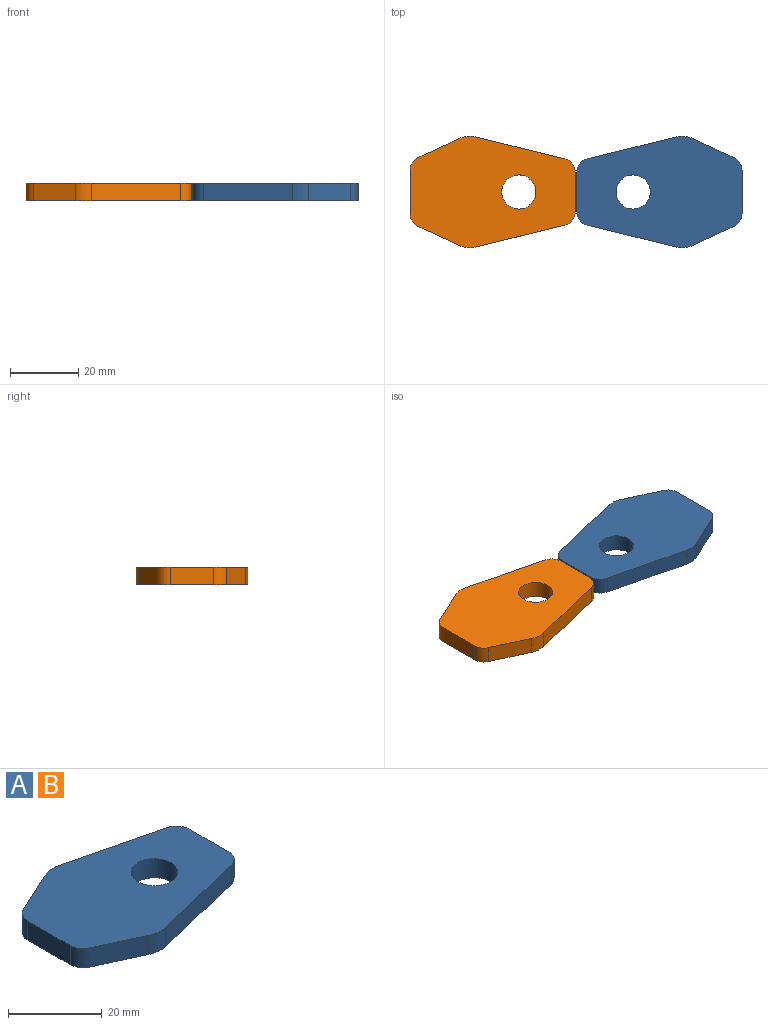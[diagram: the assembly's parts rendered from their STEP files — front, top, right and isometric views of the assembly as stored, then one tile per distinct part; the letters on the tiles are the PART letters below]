
ASSEMBLY  parts=2 mates=1
PART A: 15 faces, bbox 48.4x32.7x5 mm
  f0: cylinder r=7mm len=5mm, axis (0,0,-1), area 23.4mm2, adj f1,f7,f9,f10
  f1: plane 12.21x5.61mm, normal (-0.42,0.91,0), area 67.2mm2, adj f0,f9,f10,f11
  f2: plane 12.87x5mm, normal (-1,0,0), area 64.4mm2, adj f9,f10,f11,f12
  f3: plane 12.21x5.61mm, normal (-0.42,-0.91,0), area 67.2mm2, adj f4,f9,f10,f12
  f4: cylinder r=7mm len=5mm, axis (0,0,-1), area 23.4mm2, adj f3,f5,f9,f10
  f5: plane 26.23x6.38mm, normal (0.24,-0.97,0), area 135mm2, adj f4,f9,f10,f13
  f6: plane 11.71x5mm, normal (1,0,0), area 58.6mm2, adj f9,f10,f13,f14
  f7: plane 26.23x6.38mm, normal (0.24,0.97,0), area 135mm2, adj f0,f9,f10,f14
  f8: cylinder r=5mm len=10mm, axis (0,0,-1), area 157.1mm2, adj f9,f10
  f9: plane 48.4x32.65mm, normal (0,0,1), area 1158.1mm2, adj f0,f1,f2,f3,f4,f5,f6,f7
  f10: plane 48.4x32.65mm, normal (0,0,-1), area 1158.1mm2, adj f0,f1,f2,f3,f4,f5,f6,f7
  f11: cylinder r=4mm len=5mm, axis (0,0,1), area 22.8mm2, adj f1,f2,f9,f10
  f12: cylinder r=4mm len=5mm, axis (0,0,-1), area 22.8mm2, adj f2,f3,f9,f10
  f13: cylinder r=4mm len=5mm, axis (0,0,1), area 26.6mm2, adj f5,f6,f9,f10
  f14: cylinder r=4mm len=5mm, axis (0,0,-1), area 26.6mm2, adj f6,f7,f9,f10
PART B: same geometry as A
PLACE A rot(axis=(0,0,1),180deg) t=(48.9,0,0)mm
PLACE B at identity fixed
MATE planar B.f10 <-> A.f10  axis (0,0,-1) through (-1.34,0,0)mm
